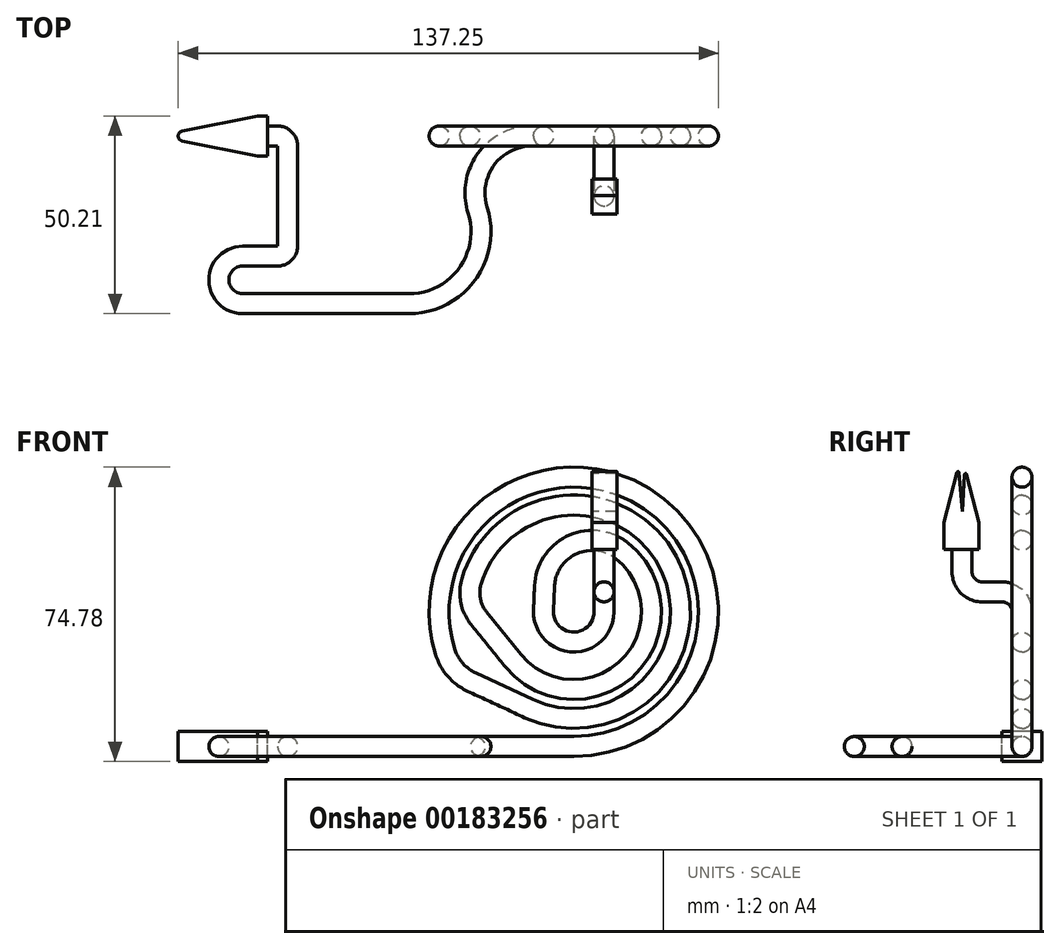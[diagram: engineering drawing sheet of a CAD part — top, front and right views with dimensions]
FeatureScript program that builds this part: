
annotation { "Feature Type Name" : "Feature", "Feature Type Description" : "" }
export const myFeature = defineFeature(function(context is Context, id is Id, definition is map)
    precondition{}
    {
        {
            var Q0;
            Q0=qCreatedBy(makeId("Right.planeOp"),FACE);
            var sketch = newSketch(context, id + "F0", { "sketchPlane" : qUnion([Q0])});
            skCircle(sketch, "E0", {"center": v(0, 0) * mm, "radius": 2.54 * mm});
            skSolve(sketch);
        }
        {
            var Q0;
            Q0=qCreatedBy(makeId("Top.planeOp"),FACE);
            var sketch = newSketch(context, id + "F1", { "sketchPlane" : qUnion([Q0])});
            skLineSegment(sketch, "E1", {"start": v(0, 0) * mm, "end": v(2.54, 0) * mm});
            skLineSegment(sketch, "E2", {"start": v(2.54, 0) * mm, "end": v(2.54, -64.55) * mm, "construction": true});
            skArc(sketch, "E3", {"start": v(5.08, -2.54) * mm, "mid": v(4.34, -0.74) * mm, "end": v(2.54, 0) * mm});
            skLineSegment(sketch, "E4", {"start": v(5.08, -2.54) * mm, "end": v(5.08, -27.94) * mm});
            skArc(sketch, "E5", {"start": v(2.54, -30.48) * mm, "mid": v(4.34, -29.74) * mm, "end": v(5.08, -27.94) * mm});
            skLineSegment(sketch, "E6", {"start": v(2.54, -30.48) * mm, "end": v(0, -30.48) * mm});
            skPoint(sketch, "E7.center.orphan", {"position": v(0, -20.32) * mm});
            skLineSegment(sketch, "E8", {"start": v(0, -30.48) * mm, "end": v(-6.35, -30.48) * mm});
            skArc(sketch, "E9", {"start": v(-6.35, -30.48) * mm, "mid": v(-12.4, -36.53) * mm, "end": v(-6.35, -42.59) * mm});
            skLineSegment(sketch, "E10", {"start": v(-6.35, -42.59) * mm, "end": v(35.88, -42.59) * mm});
            skArc(sketch, "E11", {"start": v(35.88, -42.59) * mm, "mid": v(50.64, -35.1) * mm, "end": v(53.34, -18.79) * mm});
            skArc(sketch, "E12", {"start": v(67.11, 0) * mm, "mid": v(55.47, -5.9) * mm, "end": v(53.34, -18.79) * mm});
            skLineSegment(sketch, "E13", {"start": v(67.11, 0) * mm, "end": v(77.76, 0) * mm});
            skSolve(sketch);
        }
        {
            var Q0;
            Q0=makeQuery(id+"F0.imprint","IMPRINT",FACE,{"disambiguationData":[TD([[makeQuery(id+"F0.imprint","IMPRINT",EDGE,{"derivedFrom":sQuery(id+"F0.wireOp",EDGE,"E0")}),1.0]])]});
            var Q1;
            Q1=sQuery(id+"F1.wireOp",EDGE,"E1");
            var Q2;
            Q2=sQuery(id+"F1.wireOp",EDGE,"E3");
            var Q3;
            Q3=sQuery(id+"F1.wireOp",EDGE,"E4");
            var Q4;
            Q4=sQuery(id+"F1.wireOp",EDGE,"E5");
            var Q5;
            Q5=sQuery(id+"F1.wireOp",EDGE,"E6");
            var Q6;
            Q6=sQuery(id+"F1.wireOp",EDGE,"E8");
            var Q7;
            Q7=sQuery(id+"F1.wireOp",EDGE,"E9");
            var Q8;
            Q8=sQuery(id+"F1.wireOp",EDGE,"E10");
            var Q9;
            Q9=sQuery(id+"F1.wireOp",EDGE,"E11");
            var Q10;
            Q10=sQuery(id+"F1.wireOp",EDGE,"E12");
            var Q11;
            Q11=sQuery(id+"F1.wireOp",EDGE,"E13");
            sweep(context, id + "F2", {"profiles" : qUnion([Q0]), "path" : qUnion([Q1, Q2, Q3, Q4, Q5, Q6, Q7, Q8, Q9, Q10, Q11])});
        }
        {
            var Q0;
            Q0=qCreatedBy(makeId("Top.planeOp"),FACE);
            var sketch = newSketch(context, id + "F3", { "sketchPlane" : qUnion([Q0])});
            skLineSegment(sketch, "E14.bottom", {"start": v(0, 5.08) * mm, "end": v(-2.54, 5.08) * mm});
            skLineSegment(sketch, "E14.top", {"start": v(0, -5.08) * mm, "end": v(-2.54, -5.08) * mm});
            skLineSegment(sketch, "E14.left", {"start": v(0, 5.08) * mm, "end": v(0, -5.08) * mm});
            skLineSegment(sketch, "E14.right", {"start": v(-2.54, 5.08) * mm, "end": v(-2.54, -5.08) * mm});
            skSolve(sketch);
        }
        {
            var Q0;
            Q0=makeQuery(id+"F3.imprint","IMPRINT",FACE,{"disambiguationData":[TD([[makeQuery(id+"F3.imprint","IMPRINT",EDGE,{"derivedFrom":sQuery(id+"F3.wireOp",EDGE,"E14.bottom")}),1.0]])]});
            extrude(context, id + "F4", {"entities" : qUnion([Q0]), "operationType" : NewBodyOperationType.ADD, "endBound" : BoundingType.SYMMETRIC, "oppositeDirection" : true, "depth" : 7.62 * mm});
        }
        {
            var Q0;
            Q0=makeQuery(id+"F4.opExtrude","CAP_FACE",FACE,{"disambiguationData":[OSD([sQuery(id+"F3.wireOp",EDGE,"E14.bottom"),sQuery(id+"F3.wireOp",EDGE,"E14.top"),sQuery(id+"F3.wireOp",EDGE,"E14.left"),sQuery(id+"F3.wireOp",EDGE,"E14.right")])],"isStart":true});
            var sketch = newSketch(context, id + "F5", { "sketchPlane" : qUnion([Q0])});
            skLineSegment(sketch, "E15", {"start": v(-2.54, 5.08) * mm, "end": v(-27.94, 0) * mm});
            skLineSegment(sketch, "E16", {"start": v(-27.94, 0) * mm, "end": v(-2.54, -5.08) * mm});
            skLineSegment(sketch, "E17", {"start": v(-2.54, -5.08) * mm, "end": v(-2.54, 5.08) * mm});
            skSolve(sketch);
        }
        {
            var Q0;
            Q0=makeQuery(id+"F5.imprint","IMPRINT",FACE,{"disambiguationData":[TD([[makeQuery(id+"F5.imprint","IMPRINT",EDGE,{"derivedFrom":sQuery(id+"F5.wireOp",EDGE,"E15")}),1.0]])]});
            var Q1;
            Q1=makeQuery(id+"F4.opExtrude","CAP_FACE",FACE,{"disambiguationData":[OSD([sQuery(id+"F3.wireOp",EDGE,"E14.bottom"),sQuery(id+"F3.wireOp",EDGE,"E14.top"),sQuery(id+"F3.wireOp",EDGE,"E14.left"),sQuery(id+"F3.wireOp",EDGE,"E14.right")])],"isStart":false});
            extrude(context, id + "F6", {"entities" : qUnion([Q0]), "operationType" : NewBodyOperationType.ADD, "endBound" : BoundingType.UP_TO_SURFACE, "oppositeDirection" : true, "endBoundEntityFace" : qUnion([Q1]), "depth" : 25.4 * mm});
        }
        {
            var Q0;
            Q0=makeQuery(id+"F6.opExtrude","SWEPT_EDGE",EDGE,{"disambiguationData":[OSD([sQuery(id+"F5.wireOp",EDGE,"E15"),sQuery(id+"F5.wireOp",EDGE,"E16")])]});
            fillet(context, id + "F7", {"entities" : qUnion([Q0]), "radius" : 1.27 * mm, "tangentPropagation" : true, "allowEdgeOverflow" : false});
        }
        {
            var Q0;
            Q0=qCreatedBy(makeId("Front.planeOp"),FACE);
            var sketch = newSketch(context, id + "F8", { "sketchPlane" : qUnion([Q0])});
            skLineSegment(sketch, "E18.0", {"start": v(77.76, 2.54) * mm, "end": v(77.76, -2.54) * mm});
            skPoint(sketch, "E19", {"position": v(77.76, 0) * mm});
            skArc(sketch, "E20", {"start": v(77.76, 0) * mm, "mid": v(98.08, 61.74) * mm, "end": v(45.07, 24.12) * mm});
            skArc(sketch, "E21", {"start": v(66.36, 9.62) * mm, "mid": v(102.47, 45.35) * mm, "end": v(51.79, 41.95) * mm});
            skArc(sketch, "E22", {"start": v(62.42, 21.77) * mm, "mid": v(91.87, 20.38) * mm, "end": v(89.9, 49.8) * mm});
            skArc(sketch, "E23", {"start": v(70.08, 34.52) * mm, "mid": v(77.61, 26.53) * mm, "end": v(85.45, 34.21) * mm});
            skLineSegment(sketch, "E24", {"start": v(51.86, 16.35) * mm, "end": v(66.36, 9.62) * mm});
            skLineSegment(sketch, "E25", {"start": v(53.64, 32.6) * mm, "end": v(62.42, 21.77) * mm});
            skLineSegment(sketch, "E26", {"start": v(70.33, 40.7) * mm, "end": v(70.08, 34.52) * mm});
            skPoint(sketch, "E27", {"position": v(83.5, 39.33) * mm});
            skArc(sketch, "E28", {"start": v(45.07, 24.12) * mm, "mid": v(47.64, 19.51) * mm, "end": v(51.86, 16.35) * mm});
            skArc(sketch, "E29", {"start": v(51.79, 41.95) * mm, "mid": v(51.56, 37.04) * mm, "end": v(53.64, 32.6) * mm});
            skArc(sketch, "E30", {"start": v(89.9, 49.8) * mm, "mid": v(77.33, 51.23) * mm, "end": v(70.33, 40.7) * mm});
            skLineSegment(sketch, "E31", {"start": v(77.76, 34.21) * mm, "end": v(85.45, 34.21) * mm, "construction": true});
            skPoint(sketch, "E32", {"position": v(85.45, 34.21) * mm});
            skSolve(sketch);
        }
        {
            var Q0;
            Q0=makeQuery(id+"F2.opSweep","CAP_FACE",FACE,{"disambiguationData":[OSD([sQuery(id+"F0.wireOp",EDGE,"E0"),sQuery(id+"F1.wireOp",VERTEX,"E13.end")])],"isStart":false});
            var Q1;
            Q1=sQuery(id+"F8.wireOp",EDGE,"E20");
            var Q2;
            Q2=sQuery(id+"F8.wireOp",EDGE,"E28");
            var Q3;
            Q3=sQuery(id+"F8.wireOp",EDGE,"E24");
            var Q4;
            Q4=sQuery(id+"F8.wireOp",EDGE,"E21");
            var Q5;
            Q5=sQuery(id+"F8.wireOp",EDGE,"E25");
            var Q6;
            Q6=sQuery(id+"F8.wireOp",EDGE,"E29");
            var Q7;
            Q7=sQuery(id+"F8.wireOp",EDGE,"E22");
            var Q8;
            Q8=sQuery(id+"F8.wireOp",EDGE,"E30");
            var Q9;
            Q9=sQuery(id+"F8.wireOp",EDGE,"E26");
            var Q10;
            Q10=sQuery(id+"F8.wireOp",EDGE,"E23");
            sweep(context, id + "F9", {"operationType" : NewBodyOperationType.ADD, "profiles" : qUnion([Q0]), "path" : qUnion([Q1, Q2, Q3, Q4, Q5, Q6, Q7, Q8, Q9, Q10])});
        }
        {
            var Q0;
            Q0=qCreatedBy(makeId("Right.planeOp"),FACE);
            var sketch = newSketch(context, id + "F10", { "sketchPlane" : qUnion([Q0])});
            skLineSegment(sketch, "E33.0", {"start": v(-2.54, 34.21) * mm, "end": v(2.54, 34.21) * mm});
            skPoint(sketch, "E34", {"position": v(0, 34.21) * mm});
            skArc(sketch, "E35", {"start": v(0, 34.21) * mm, "mid": v(-1.49, 37.8) * mm, "end": v(-5.08, 39.3) * mm});
            skLineSegment(sketch, "E36", {"start": v(-5.08, 39.3) * mm, "end": v(-10.16, 39.3) * mm});
            skArc(sketch, "E37", {"start": v(-15.24, 44.37) * mm, "mid": v(-13.75, 40.78) * mm, "end": v(-10.16, 39.3) * mm});
            skLineSegment(sketch, "E38", {"start": v(-15.24, 44.37) * mm, "end": v(-15.24, 50.12) * mm});
            skSolve(sketch);
        }
        {
            var Q0;
            Q0=makeQuery(id+"F9.opSweep","CAP_FACE",FACE,{"disambiguationData":[OSD([sQuery(id+"F0.wireOp",EDGE,"E0"),sQuery(id+"F1.wireOp",VERTEX,"E13.end"),sQuery(id+"F8.wireOp",VERTEX,"E23.end")])],"isStart":false});
            var Q1;
            Q1=sQuery(id+"F10.wireOp",EDGE,"E35");
            var Q2;
            Q2=sQuery(id+"F10.wireOp",EDGE,"E36");
            var Q3;
            Q3=sQuery(id+"F10.wireOp",EDGE,"E37");
            var Q4;
            Q4=sQuery(id+"F10.wireOp",EDGE,"E38");
            sweep(context, id + "F11", {"operationType" : NewBodyOperationType.ADD, "profiles" : qUnion([Q0]), "path" : qUnion([Q1, Q2, Q3, Q4])});
        }
        {
            var Q0;
            Q0=qCreatedBy(makeId("Right.planeOp"),FACE);
            cPlane(context, id + "F12", {"entities" : qUnion([Q0]), "cplaneType" : CPlaneType.OFFSET, "offset" : 85.6 * mm, "width" : 152.4 * mm, "height" : 152.4 * mm});
        }
        {
            var Q0;
            Q0=qCreatedBy(id+"F12.planeOp",FACE);
            var sketch = newSketch(context, id + "F13", { "sketchPlane" : qUnion([Q0])});
            skLineSegment(sketch, "E39.0", {"start": v(-17.78, 50.12) * mm, "end": v(-12.7, 50.12) * mm});
            skLineSegment(sketch, "E40.bottom", {"start": v(-19.78, 50.12) * mm, "end": v(-10.93, 50.12) * mm});
            skLineSegment(sketch, "E40.top", {"start": v(-19.78, 56.9) * mm, "end": v(-10.93, 56.9) * mm});
            skLineSegment(sketch, "E40.left", {"start": v(-19.78, 50.12) * mm, "end": v(-19.78, 56.9) * mm});
            skLineSegment(sketch, "E40.right", {"start": v(-10.93, 50.12) * mm, "end": v(-10.93, 56.9) * mm});
            skLineSegment(sketch, "E41", {"start": v(-19.78, 56.9) * mm, "end": v(-16.14, 71.05) * mm});
            skLineSegment(sketch, "E42", {"start": v(-14.49, 70.74) * mm, "end": v(-10.93, 56.9) * mm});
            skLineSegment(sketch, "E43", {"start": v(-16.14, 71.05) * mm, "end": v(-15.12, 59.77) * mm});
            skLineSegment(sketch, "E44", {"start": v(-15.12, 59.77) * mm, "end": v(-14.49, 70.74) * mm});
            skSolve(sketch);
        }
        {
            var Q0;
            Q0=makeQuery(id+"F13.imprint","IMPRINT",FACE,{"disambiguationData":[TD([[makeQuery(id+"F13.imprint","IMPRINT",EDGE,{"derivedFrom":sQuery(id+"F13.wireOp",EDGE,"E40.top")}),-1.0]])]});
            var Q1;
            Q1=makeQuery(id+"F13.imprint","IMPRINT",FACE,{"disambiguationData":[TD([[makeQuery(id+"F13.imprint","IMPRINT",EDGE,{"derivedFrom":sQuery(id+"F13.wireOp",EDGE,"E40.top")}),1.0]])]});
            extrude(context, id + "F14", {"entities" : qUnion([Q0, Q1]), "operationType" : NewBodyOperationType.ADD, "endBound" : BoundingType.SYMMETRIC, "depth" : 6.35 * mm});
        }
        {
            var Q0;
            Q0=makeQuery(id+"F14.opExtrude","SWEPT_EDGE",EDGE,{"disambiguationData":[OSD([sQuery(id+"F13.wireOp",EDGE,"E41"),sQuery(id+"F13.wireOp",EDGE,"E43")])]});
            var Q1;
            Q1=makeQuery(id+"F14.opExtrude","SWEPT_EDGE",EDGE,{"disambiguationData":[OSD([sQuery(id+"F13.wireOp",EDGE,"E42"),sQuery(id+"F13.wireOp",EDGE,"E44")])]});
            fillet(context, id + "F15", {"entities" : qUnion([Q0, Q1]), "radius" : 0.25 * mm, "tangentPropagation" : true, "allowEdgeOverflow" : false});
        }
    });
